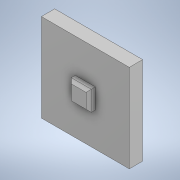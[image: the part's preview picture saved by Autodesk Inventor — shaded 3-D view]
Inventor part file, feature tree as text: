
AUTODESK INVENTOR PART (.ipt)
format: ipt  version: 2022 (Build 260153000, 153)  size: 184,320 bytes
history: native  units: in
note: dims shown in document units (in); Inventor stores cm internally (conversion verified against a paired STEP export)
features: extrude x2, sketch x2, chamfer x1
ambient origin geometry x8: Origin, YZ Plane, XZ Plane, XY Plane, X Axis, Y Axis, Z Axis, Center Point
bodies: Solid1 (feature_tree), Body2 (feature_tree)
feature tree (5):
  extrude  "Extrusion1"  Depth=0.0295in
  extrude  "Extrusion2"  Depth=0.0098in TaperAngle=0.0deg
  chamfer  "Chamfer1"  Distance=0.0039in Angle=45.0deg
  sketch  "Sketch1"  dims[d0=0.2313in d1=0.0in d2=0.0295in]
  sketch  "Sketch3"  dims[d3=0.0295in d4=0.0098in d5=0.0in d6=0.0039in d7=0.0787in d8=45.0deg]
